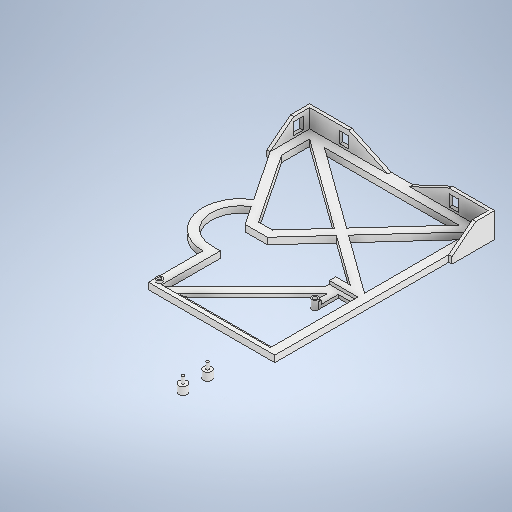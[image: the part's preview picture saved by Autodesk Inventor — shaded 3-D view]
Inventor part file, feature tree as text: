
AUTODESK INVENTOR PART (.ipt)
format: ipt  version: 2025.2 (Build 292293000, 293)  size: 451,584 bytes
history: native  units: mm
features: extrude x8, sketch x6
ambient origin geometry x8: Origin, YZ Plane, XZ Plane, XY Plane, X Axis, Y Axis, Z Axis, Center Point
bodies: Solid1 (feature_tree)
feature tree (14):
  sketch  "Sketch1"  dims[d0=52.786mm d1=82.0mm]
  extrude  "Extrusion1"  Depth=82.0mm
  extrude  "Extrusion2"  Depth=5.0mm
  extrude  "Extrusion3"  Depth=58.0mm
  extrude  "Extrusion4"  Depth=25.0mm
  extrude  "Extrusion5"  Depth=10.23mm
  extrude  "Extrusion6"  Depth=17.153mm
  extrude  "Extrusion7"  Depth=3.0mm
  extrude  "Extrusion8"  Depth=25.0mm
  sketch  "Sketch4"  dims[d2=18.104mm d3=5.0mm]
  sketch  "Sketch5"  dims[d4=40.214mm d5=58.0mm]
  sketch  "Sketch6"  dims[d6=25.0mm d7=25.52195mm]
  sketch  "Sketch7"  dims[d8=41.72mm d9=10.23mm]
  sketch  "Sketch8"  dims[d12=4.0mm d13=17.153mm d14=27.568mm d15=25.0mm d16=13.153mm d17=4.0mm d18=0.0mm d19=4.0mm d20=6.808mm d21=83.035mm d22=13.14mm d23=5.0mm d24=4.0mm d25=9.214mm d26=3.19mm d27=2.9mm d28=1.8mm d29=3.0mm d30=2.0mm d31=2.9mm d32=1.8mm d33=4.0mm d34=3.0mm d35=0.0mm d36=4.0mm d37=0.0mm d38=2.0mm d39=0.0mm d40=2.0mm d41=7.75mm d42=1.5mm d43=0.0mm d44=8.5mm d45=17.94mm d46=20.0mm d47=2.3mm d48=2.3mm d49=5.2mm d50=4.2mm d51=1.5mm d52=0.0mm d53=19.604mm d55=13.826mm d56=1.5mm d57=0.0mm d58=13.826mm d59=4.5mm d60=5.5mm d61=2.0mm d62=4.5mm d63=1.5mm d64=0.0mm d65=3.5mm d66=0.0mm d67=1.3mm d68=1.35mm d69=3.0mm d70=0.0mm]
